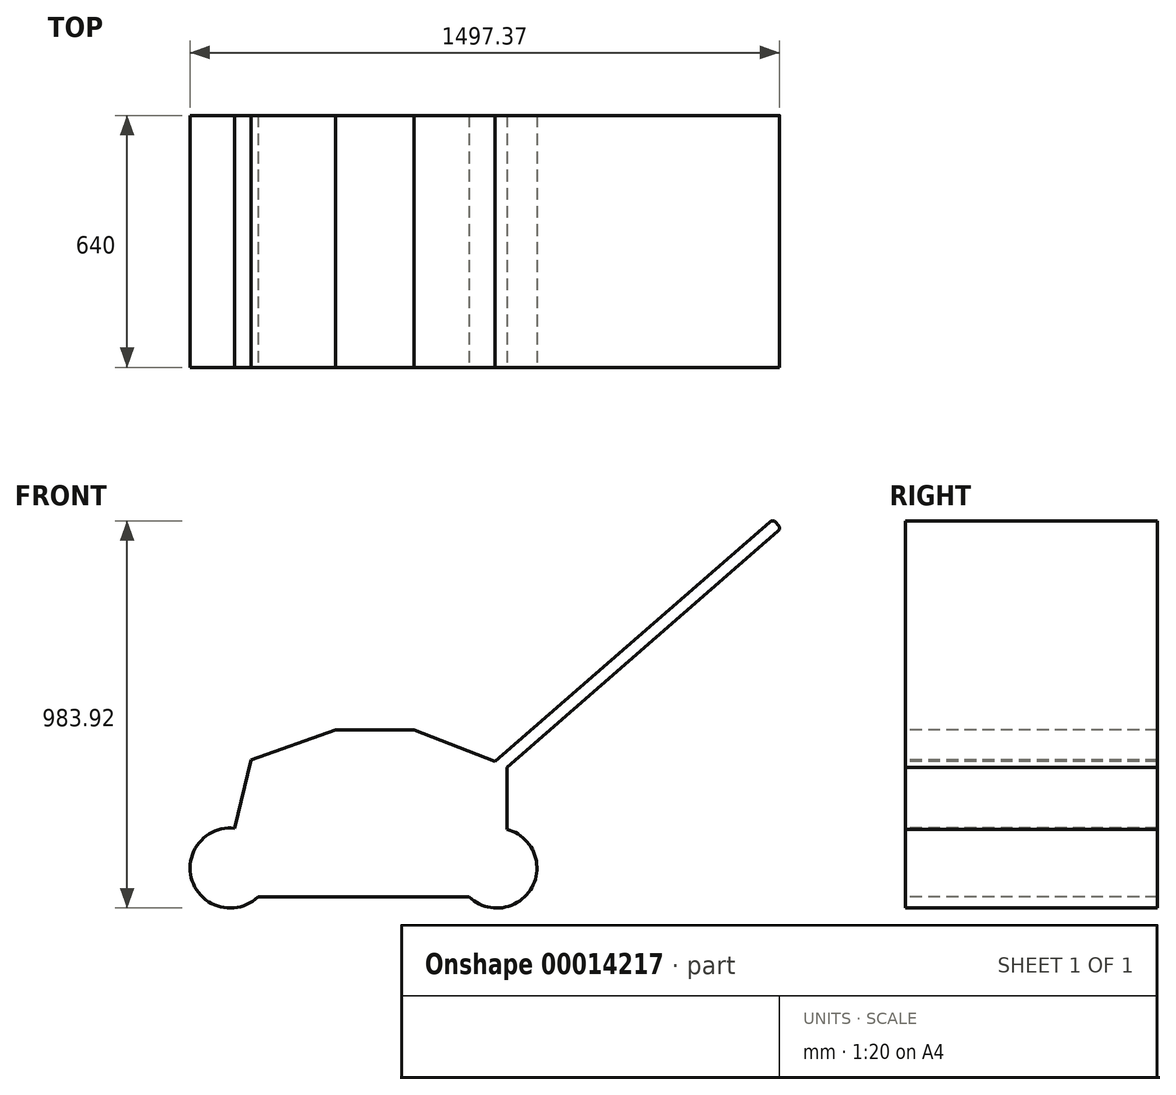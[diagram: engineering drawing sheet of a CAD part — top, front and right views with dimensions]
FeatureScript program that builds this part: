
annotation { "Feature Type Name" : "Feature", "Feature Type Description" : "" }
export const myFeature = defineFeature(function(context is Context, id is Id, definition is map)
    precondition{}
    {
        {
            var Q0;
            Q0=qCreatedBy(makeId("Front.planeOp"),FACE);
            var sketch = newSketch(context, id + "F0", { "sketchPlane" : qUnion([Q0])});
            skArc(sketch, "E0", {"start": v(288.94, 855.5) * mm, "mid": v(180.72, 722.15) * mm, "end": v(347.57, 681.5) * mm});
            skArc(sketch, "E1", {"start": v(884.48, 681.5) * mm, "mid": v(1043.8, 705.14) * mm, "end": v(980.08, 853.07) * mm});
            skLineSegment(sketch, "E2", {"start": v(288.94, 855.5) * mm, "end": v(330.45, 1029.33) * mm});
            skLineSegment(sketch, "E3", {"start": v(330.45, 1029.33) * mm, "end": v(544.54, 1105.06) * mm});
            skLineSegment(sketch, "E4", {"start": v(544.54, 1105.06) * mm, "end": v(743.83, 1105.06) * mm});
            skLineSegment(sketch, "E5", {"start": v(743.83, 1105.06) * mm, "end": v(950.52, 1025.91) * mm});
            skLineSegment(sketch, "E6", {"start": v(950.52, 1025.91) * mm, "end": v(1648.92, 1634.46) * mm});
            skLineSegment(sketch, "E7", {"start": v(1663.03, 1633.49) * mm, "end": v(1670.31, 1625.13) * mm});
            skLineSegment(sketch, "E8", {"start": v(1669.34, 1611.02) * mm, "end": v(980.08, 1010.44) * mm});
            skLineSegment(sketch, "E9", {"start": v(980.08, 1010.44) * mm, "end": v(980.08, 853.07) * mm});
            skLineSegment(sketch, "E10", {"start": v(884.48, 681.5) * mm, "end": v(343.18, 681.5) * mm});
            skPoint(sketch, "E11.visualSharp", {"position": v(1656.46, 1641.03) * mm});
            skArc(sketch, "E11.filletArc", {"start": v(1663.03, 1633.49) * mm, "mid": v(1656.17, 1636.9) * mm, "end": v(1648.92, 1634.46) * mm});
            skPoint(sketch, "E12.visualSharp", {"position": v(1676.88, 1617.59) * mm});
            skArc(sketch, "E12.filletArc", {"start": v(1669.34, 1611.02) * mm, "mid": v(1672.75, 1617.87) * mm, "end": v(1670.31, 1625.13) * mm});
            skSolve(sketch);
        }
        {
            var Q0;
            {var subQ1=sQuery(id+"F0.wireOp",EDGE,"E0");Q0=makeQuery(id+"F0.imprint","IMPRINT",FACE,{"disambiguationData":[TD([[makeQuery(id+"F0.imprint","IMPRINT",EDGE,{"derivedFrom":subQ1}),1.0]])]});}
            extrude(context, id + "F1", {"entities" : qUnion([Q0]), "oppositeDirection" : true, "depth" : 640 * mm});
        }
    });
